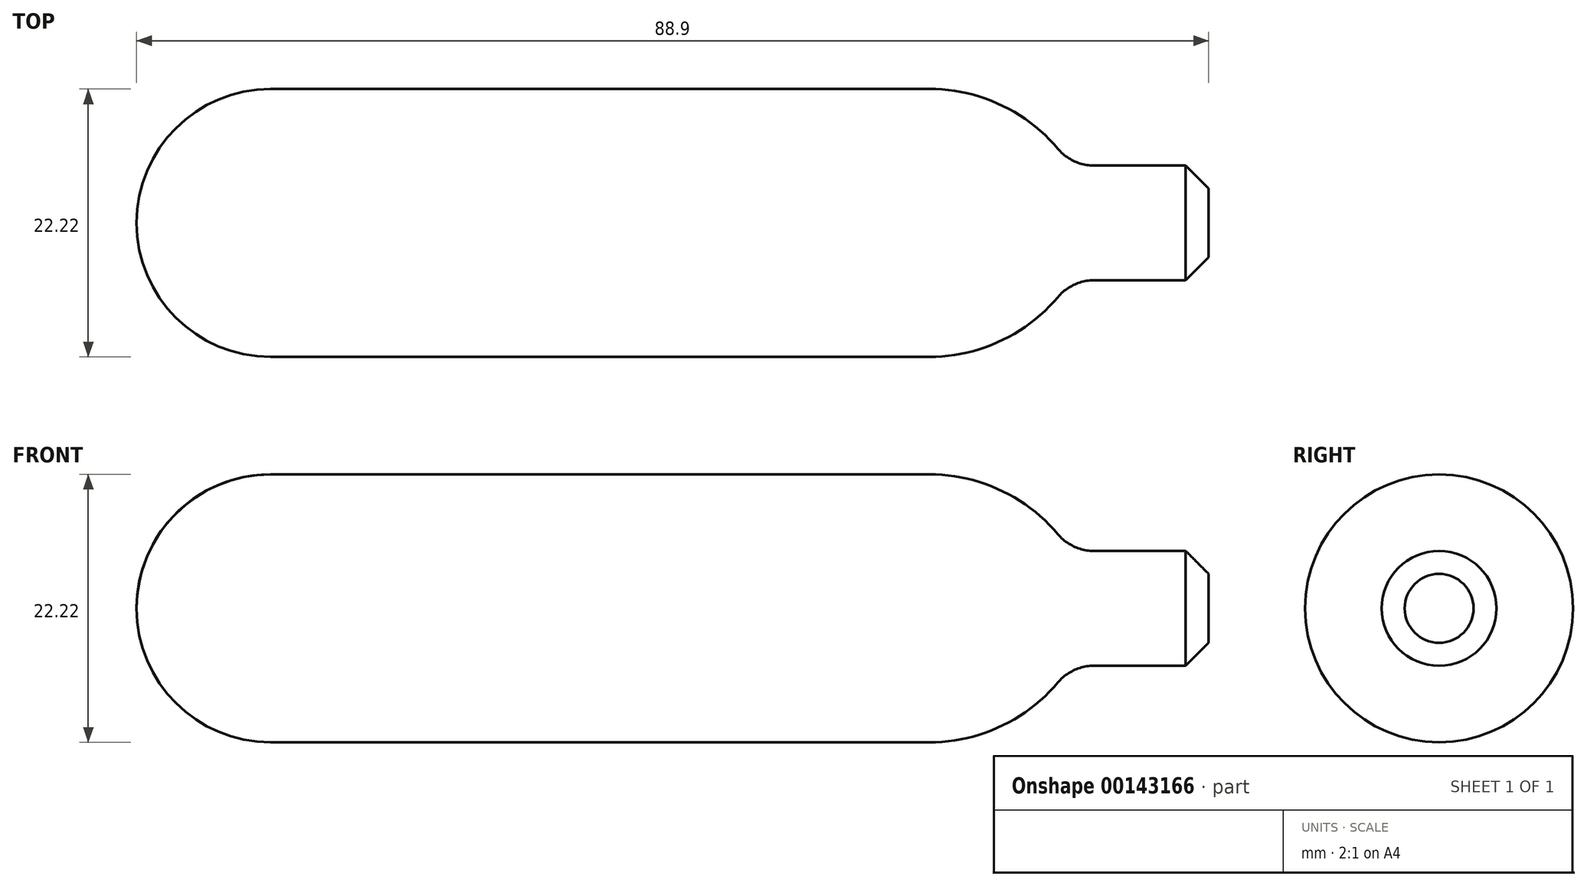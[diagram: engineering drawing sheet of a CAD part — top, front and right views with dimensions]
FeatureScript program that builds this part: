
annotation { "Feature Type Name" : "Feature", "Feature Type Description" : "" }
export const myFeature = defineFeature(function(context is Context, id is Id, definition is map)
    precondition{}
    {
        {
            var Q0;
            Q0=qCreatedBy(makeId("Front.planeOp"),FACE);
            var sketch = newSketch(context, id + "F0", { "sketchPlane" : qUnion([Q0])});
            skLineSegment(sketch, "E0", {"start": v(-88.9, 0) * mm, "end": v(0, 0) * mm});
            skLineSegment(sketch, "E1", {"start": v(0, 0) * mm, "end": v(0, 2.86) * mm});
            skLineSegment(sketch, "E2", {"start": v(0, 2.86) * mm, "end": v(-1.9, 4.76) * mm});
            skLineSegment(sketch, "E3", {"start": v(-1.9, 4.76) * mm, "end": v(-9.53, 4.76) * mm});
            skArc(sketch, "E4", {"start": v(-9.53, 4.76) * mm, "mid": v(-11.16, 5.12) * mm, "end": v(-12.5, 6.14) * mm});
            skArc(sketch, "E5", {"start": v(-12.5, 6.14) * mm, "mid": v(-17.29, 9.8) * mm, "end": v(-23.18, 11.11) * mm});
            skLineSegment(sketch, "E6", {"start": v(-23.18, 11.11) * mm, "end": v(-77.79, 11.11) * mm});
            skArc(sketch, "E7", {"start": v(-77.79, 11.11) * mm, "mid": v(-85.65, 7.86) * mm, "end": v(-88.9, 0) * mm});
            skLineSegment(sketch, "E8", {"start": v(-88.9, 0) * mm, "end": v(-88.9, -10.27) * mm, "construction": true});
            skSolve(sketch);
        }
        {
            var Q0;
            Q0=makeQuery(id+"F0.imprint","IMPRINT",FACE,{"disambiguationData":[TD([[makeQuery(id+"F0.imprint","IMPRINT",EDGE,{"derivedFrom":sQuery(id+"F0.wireOp",EDGE,"E0")}),1.0]])]});
            var Q1;
            Q1=sQuery(id+"F0.wireOp",EDGE,"E0");
            revolve(context, id + "F1", {"entities" : qUnion([Q0]), "axis" : qUnion([Q1]), "revolveType" : RevolveType.FULL});
        }
    });
